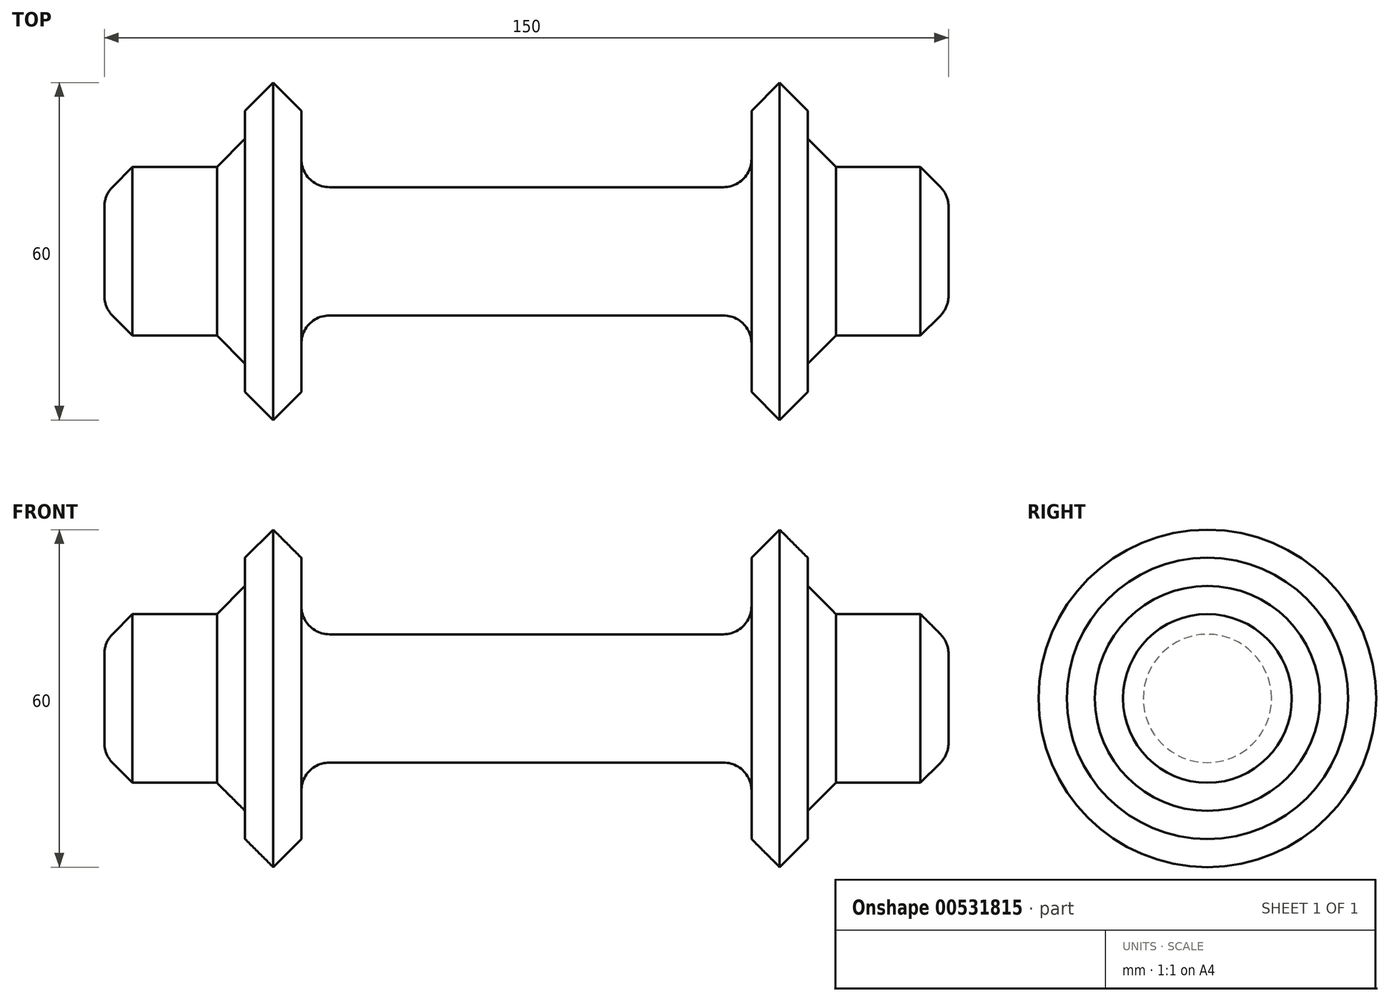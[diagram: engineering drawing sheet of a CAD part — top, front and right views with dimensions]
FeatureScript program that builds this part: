
annotation { "Feature Type Name" : "Feature", "Feature Type Description" : "" }
export const myFeature = defineFeature(function(context is Context, id is Id, definition is map)
    precondition{}
    {
        {
            var Q0;
            Q0=qCreatedBy(makeId("Front.planeOp"),FACE);
            var sketch = newSketch(context, id + "F0", { "sketchPlane" : qUnion([Q0])});
            skLineSegment(sketch, "E0", {"start": v(0, 0) * mm, "end": v(0, 11.4) * mm});
            skLineSegment(sketch, "E1", {"start": v(0, 11.4) * mm, "end": v(35, 11.4) * mm});
            skLineSegment(sketch, "E2", {"start": v(40, 16.4) * mm, "end": v(40, 30) * mm});
            skLineSegment(sketch, "E3", {"start": v(40, 30) * mm, "end": v(50, 30) * mm});
            skLineSegment(sketch, "E4", {"start": v(50, 30) * mm, "end": v(50, 15) * mm});
            skLineSegment(sketch, "E5", {"start": v(50, 15) * mm, "end": v(75, 15) * mm});
            skLineSegment(sketch, "E6", {"start": v(75, 15) * mm, "end": v(75, 0) * mm});
            skLineSegment(sketch, "E7", {"start": v(75, 0) * mm, "end": v(0, 0) * mm});
            skPoint(sketch, "E8.visualSharp", {"position": v(40, 11.4) * mm});
            skArc(sketch, "E8.filletArc", {"start": v(35, 11.4) * mm, "mid": v(38.54, 12.87) * mm, "end": v(40, 16.4) * mm});
            skSolve(sketch);
        }
        {
            var Q0;
            Q0 = qSketchRegion(id + "F0", true);
            var Q1;
            Q1=sQuery(id+"F0.wireOp",EDGE,"E7");
            revolve(context, id + "F1", {"entities" : qUnion([Q0]), "axis" : qUnion([Q1]), "revolveType" : RevolveType.FULL});
        }
        {
            var Q0;
            Q0=makeQuery(id+"F1.opRevolve","SWEPT_BODY",BODY,{"disambiguationData":[OSD([sQuery(id+"F0.wireOp",EDGE,"E0"),sQuery(id+"F0.wireOp",EDGE,"E1"),sQuery(id+"F0.wireOp",EDGE,"E2"),sQuery(id+"F0.wireOp",EDGE,"E3"),sQuery(id+"F0.wireOp",EDGE,"E4"),sQuery(id+"F0.wireOp",EDGE,"E5"),sQuery(id+"F0.wireOp",EDGE,"E6"),sQuery(id+"F0.wireOp",EDGE,"E7"),sQuery(id+"F0.wireOp",EDGE,"E8.filletArc")])]});
            var Q1;
            Q1=makeQuery(id+"F1.opRevolve","SWEPT_FACE",FACE,{"disambiguationData":[OSD([sQuery(id+"F0.wireOp",EDGE,"E0")])]});
            mirror(context, id + "F2", {"operationType" : NewBodyOperationType.ADD, "entities" : qUnion([Q0]), "mirrorPlane" : qUnion([Q1])});
        }
        {
            var Q0;
            Q0=makeQuery(id+"F2.opPattern","COPY",EDGE,{"derivedFrom":makeQuery(id+"F1.opRevolve","SWEPT_EDGE",EDGE,{"disambiguationData":[OSD([sQuery(id+"F0.wireOp",EDGE,"E2"),sQuery(id+"F0.wireOp",EDGE,"E3")])]}),"instanceName":"1"});
            var Q1;
            Q1=makeQuery(id+"F2.opPattern","COPY",EDGE,{"derivedFrom":makeQuery(id+"F1.opRevolve","SWEPT_EDGE",EDGE,{"disambiguationData":[OSD([sQuery(id+"F0.wireOp",EDGE,"E5"),sQuery(id+"F0.wireOp",EDGE,"E6")])]}),"instanceName":"1"});
            var Q2;
            Q2=makeQuery(id+"F2.opPattern","COPY",EDGE,{"derivedFrom":makeQuery(id+"F1.opRevolve","SWEPT_EDGE",EDGE,{"disambiguationData":[OSD([sQuery(id+"F0.wireOp",EDGE,"E3"),sQuery(id+"F0.wireOp",EDGE,"E4")])]}),"instanceName":"1"});
            var Q3;
            Q3=makeQuery(id+"F1.opRevolve","SWEPT_EDGE",EDGE,{"disambiguationData":[OSD([sQuery(id+"F0.wireOp",EDGE,"E2"),sQuery(id+"F0.wireOp",EDGE,"E3")])]});
            var Q4;
            Q4=makeQuery(id+"F1.opRevolve","SWEPT_EDGE",EDGE,{"disambiguationData":[OSD([sQuery(id+"F0.wireOp",EDGE,"E2"),sQuery(id+"F0.wireOp",EDGE,"E8.filletArc")])]});
            var Q5;
            Q5=makeQuery(id+"F2.opPattern","COPY",EDGE,{"derivedFrom":makeQuery(id+"F1.opRevolve","SWEPT_EDGE",EDGE,{"disambiguationData":[OSD([sQuery(id+"F0.wireOp",EDGE,"E1"),sQuery(id+"F0.wireOp",EDGE,"E8.filletArc")])]}),"instanceName":"1"});
            var Q6;
            Q6=makeQuery(id+"F1.opRevolve","SWEPT_EDGE",EDGE,{"disambiguationData":[OSD([sQuery(id+"F0.wireOp",EDGE,"E1"),sQuery(id+"F0.wireOp",EDGE,"E8.filletArc")])]});
            var Q7;
            Q7=makeQuery(id+"F1.opRevolve","SWEPT_EDGE",EDGE,{"disambiguationData":[OSD([sQuery(id+"F0.wireOp",EDGE,"E5"),sQuery(id+"F0.wireOp",EDGE,"E6")])]});
            var Q8;
            Q8=makeQuery(id+"F1.opRevolve","SWEPT_EDGE",EDGE,{"disambiguationData":[OSD([sQuery(id+"F0.wireOp",EDGE,"E3"),sQuery(id+"F0.wireOp",EDGE,"E4")])]});
            var Q9;
            Q9=makeQuery(id+"F2.opPattern","COPY",EDGE,{"derivedFrom":makeQuery(id+"F1.opRevolve","SWEPT_EDGE",EDGE,{"disambiguationData":[OSD([sQuery(id+"F0.wireOp",EDGE,"E2"),sQuery(id+"F0.wireOp",EDGE,"E8.filletArc")])]}),"instanceName":"1"});
            var Q10;
            Q10=makeQuery(id+"F2.opPattern","COPY",EDGE,{"derivedFrom":makeQuery(id+"F1.opRevolve","SWEPT_EDGE",EDGE,{"disambiguationData":[OSD([sQuery(id+"F0.wireOp",EDGE,"E4"),sQuery(id+"F0.wireOp",EDGE,"E5")])]}),"instanceName":"1"});
            var Q11;
            Q11=makeQuery(id+"F1.opRevolve","SWEPT_EDGE",EDGE,{"disambiguationData":[OSD([sQuery(id+"F0.wireOp",EDGE,"E4"),sQuery(id+"F0.wireOp",EDGE,"E5")])]});
            chamfer(context, id + "F3", {"entities" : qUnion([Q0, Q1, Q2, Q3, Q4, Q5, Q6, Q7, Q8, Q9, Q10, Q11]), "width" : 5 * mm, "tangentPropagation" : true});
        }
        {
            var Q0;
            Q0=makeQuery(id+"F2.opPattern","COPY",FACE,{"derivedFrom":makeQuery(id+"F1.opRevolve","SWEPT_FACE",FACE,{"disambiguationData":[OSD([sQuery(id+"F0.wireOp",EDGE,"E6")])]}),"instanceName":"1"});
            var Q1;
            {var subQ0=sQuery(id+"F0.wireOp",EDGE,"E6");Q1=makeQuery(id+"F3.opChamfer","BLEND_EDGE",EDGE,{"blendedFrom":[makeQuery(id+"F1.opRevolve","SWEPT_EDGE",EDGE,{"disambiguationData":[OSD([sQuery(id+"F0.wireOp",EDGE,"E5"),subQ0])]}),makeQuery(id+"F1.opRevolve","SWEPT_FACE",FACE,{"disambiguationData":[OSD([subQ0])]})],"blendedInto":[makeQuery(id+"F1.opRevolve","SWEPT_FACE",FACE,{"disambiguationData":[OSD([subQ0])]})]});}
            fillet(context, id + "F4", {"entities" : qUnion([Q0, Q1]), "radius" : 5 * mm, "tangentPropagation" : true, "allowEdgeOverflow" : false});
        }
    });
